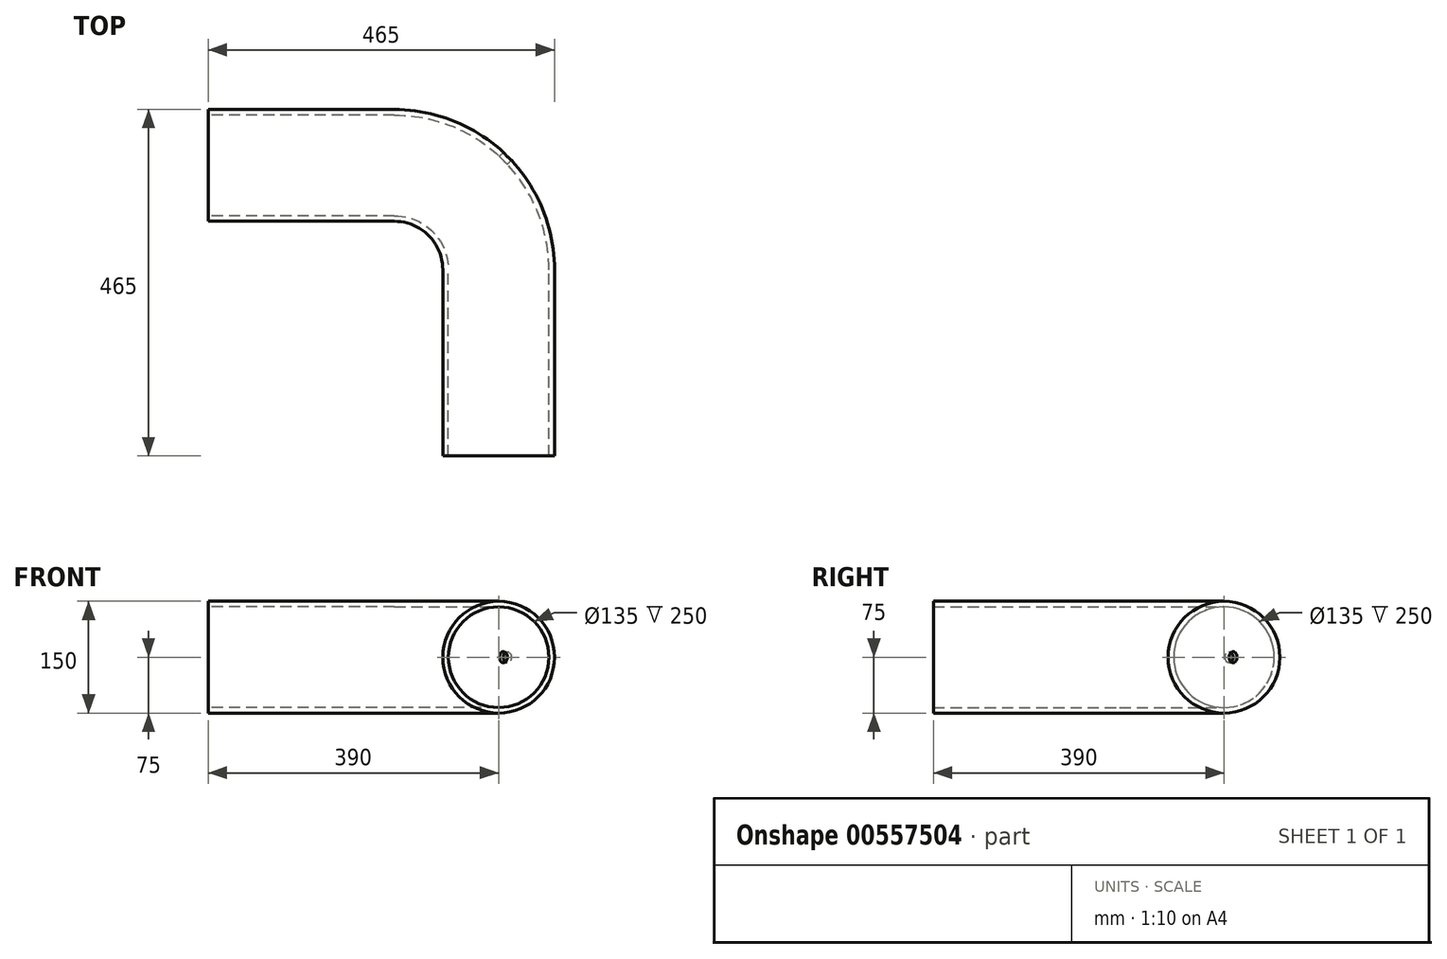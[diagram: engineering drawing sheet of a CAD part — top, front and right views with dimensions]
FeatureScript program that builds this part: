
annotation { "Feature Type Name" : "Feature", "Feature Type Description" : "" }
export const myFeature = defineFeature(function(context is Context, id is Id, definition is map)
    precondition{}
    {
        {
            var Q0;
            Q0=qCreatedBy(makeId("Front.planeOp"),FACE);
            var sketch = newSketch(context, id + "F0", { "sketchPlane" : qUnion([Q0])});
            skCircle(sketch, "E0", {"center": v(0, 0) * mm, "radius": 75 * mm});
            skCircle(sketch, "E1", {"center": v(0, 0) * mm, "radius": 67.5 * mm});
            skSolve(sketch);
        }
        {
            var Q0;
            Q0=qCreatedBy(makeId("Top.planeOp"),FACE);
            var sketch = newSketch(context, id + "F1", { "sketchPlane" : qUnion([Q0])});
            skLineSegment(sketch, "E2", {"start": v(0, 0) * mm, "end": v(0, 250) * mm});
            skLineSegment(sketch, "E3", {"start": v(-245, 390) * mm, "end": v(-390, 390) * mm});
            skPoint(sketch, "E4.visualSharp", {"position": v(0, 390) * mm});
            skLineSegment(sketch, "E5", {"start": v(-140, 390) * mm, "end": v(-390, 390) * mm});
            skLineSegment(sketch, "E6", {"start": v(0, 250) * mm, "end": v(0, 250) * mm});
            skArc(sketch, "E7.filletArc", {"start": v(0, 250) * mm, "mid": v(-41, 349) * mm, "end": v(-140, 390) * mm});
            skSolve(sketch);
        }
        {
            var Q0;
            Q0=makeQuery(id+"F0.imprint","IMPRINT",FACE,{"disambiguationData":[TD([[makeQuery(id+"F0.imprint","IMPRINT",EDGE,{"derivedFrom":sQuery(id+"F0.wireOp",EDGE,"E0")}),1.0]])]});
            var Q1;
            Q1=sQuery(id+"F1.wireOp",EDGE,"E2");
            var Q2;
            Q2=sQuery(id+"F1.wireOp",EDGE,"E7.filletArc");
            var Q3;
            Q3=sQuery(id+"F1.wireOp",EDGE,"E5");
            sweep(context, id + "F2", {"profiles" : qUnion([Q0]), "path" : qUnion([Q1, Q2, Q3])});
        }
        {
            var Q0;
            Q0=makeQuery(id+"F2.opSweep","SWEPT_FACE",FACE,{"disambiguationData":[OSD([sQuery(id+"F0.wireOp",EDGE,"E0"),sQuery(id+"F1.wireOp",EDGE,"E7.filletArc")])]});
            cPlane(context, id + "F3", {"entities" : qUnion([Q0]), "cplaneType" : CPlaneType.LINE_ANGLE, "offset" : 25 * mm, "angle" : 45 * degree, "width" : 150 * mm, "height" : 150 * mm});
        }
        {
            var Q0;
            Q0=qCreatedBy(id+"F3.planeOp",FACE);
            cPlane(context, id + "F4", {"entities" : qUnion([Q0]), "cplaneType" : CPlaneType.OFFSET, "offset" : 300 * mm, "width" : 150 * mm, "height" : 150 * mm});
        }
        {
            var Q0;
            Q0=qCreatedBy(id+"F4.planeOp",FACE);
            var sketch = newSketch(context, id + "F5", { "sketchPlane" : qUnion([Q0])});
            skCircle(sketch, "E8", {"center": v(276.1, 0) * mm, "radius": 7.5 * mm});
            skSolve(sketch);
        }
        {
            var Q0;
            Q0 = qSketchRegion(id + "F5", true);
            extrude(context, id + "F6", {"entities" : qUnion([Q0]), "operationType" : NewBodyOperationType.REMOVE, "oppositeDirection" : true, "depth" : 150 * mm, "offsetDistance" : 25 * mm});
        }
    });
